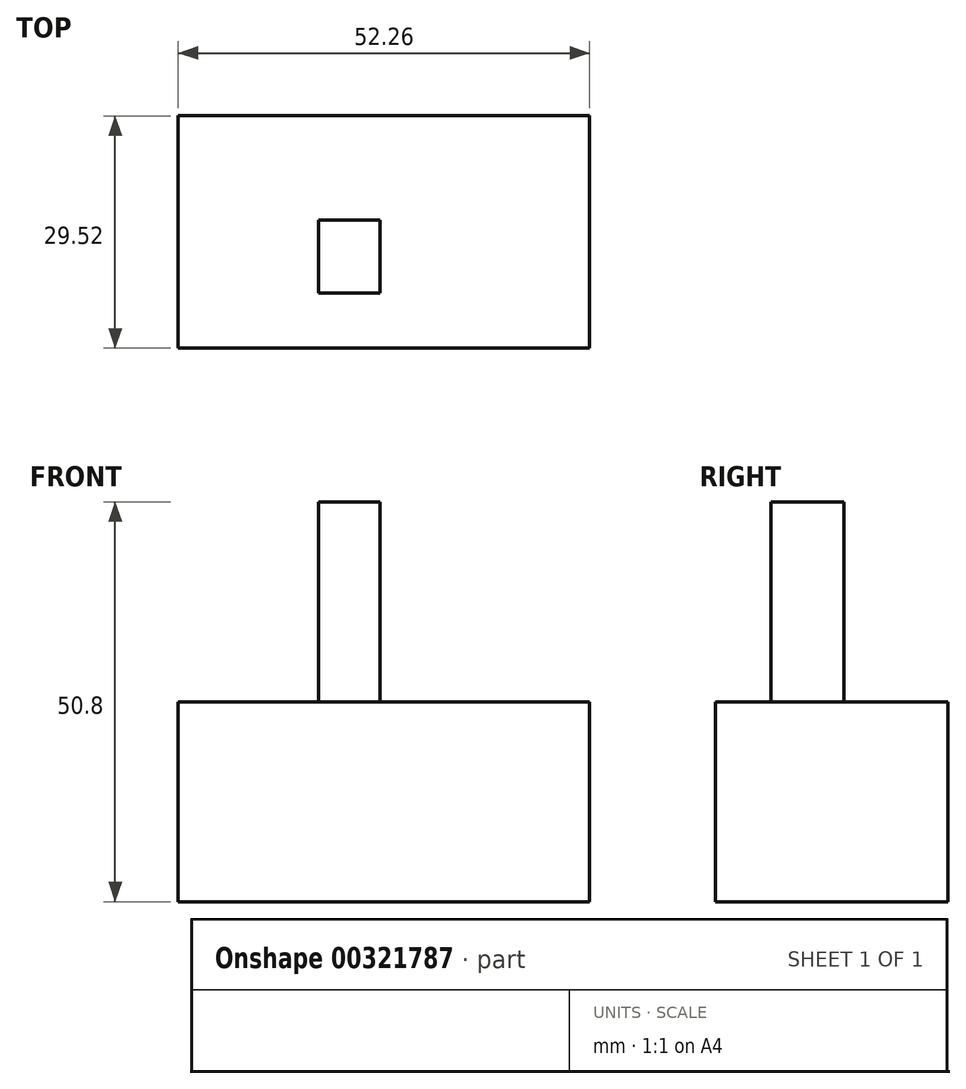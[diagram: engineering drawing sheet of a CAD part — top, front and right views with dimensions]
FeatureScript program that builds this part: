
annotation { "Feature Type Name" : "Feature", "Feature Type Description" : "" }
export const myFeature = defineFeature(function(context is Context, id is Id, definition is map)
    precondition{}
    {
        {
            var Q0;
            Q0=qCreatedBy(makeId("Top.planeOp"),FACE);
            var sketch = newSketch(context, id + "F0", { "sketchPlane" : qUnion([Q0])});
            skLineSegment(sketch, "E0.bottom", {"start": v(0, 0) * mm, "end": v(52.26, 0) * mm});
            skLineSegment(sketch, "E0.top", {"start": v(0, 29.52) * mm, "end": v(52.26, 29.52) * mm});
            skLineSegment(sketch, "E0.left", {"start": v(0, 0) * mm, "end": v(0, 29.52) * mm});
            skLineSegment(sketch, "E0.right", {"start": v(52.26, 0) * mm, "end": v(52.26, 29.52) * mm});
            skSolve(sketch);
        }
        {
            var Q0;
            Q0 = qSketchRegion(id + "F0", true);
            extrude(context, id + "F1", {"entities" : qUnion([Q0]), "depth" : 25.4 * mm});
        }
        {
            var Q0;
            Q0=makeQuery(id+"F1.opExtrude","CAP_FACE",FACE,{"disambiguationData":[OSD([sQuery(id+"F0.wireOp",EDGE,"E0.bottom"),sQuery(id+"F0.wireOp",EDGE,"E0.top"),sQuery(id+"F0.wireOp",EDGE,"E0.left"),sQuery(id+"F0.wireOp",EDGE,"E0.right")])],"isStart":false});
            var sketch = newSketch(context, id + "F2", { "sketchPlane" : qUnion([Q0])});
            skText(sketch, "E1", { "text": "諺呈\n", "fontName": "OpenSans-Regular.ttf"});
            const initialGuessF2  = {"E1": [0.00797, 0.0062, 1, 0, 0.01092]};
            skSetInitialGuess(sketch, initialGuessF2);
            skSolve(sketch);
        }
        {
            var Q0;
            Q0=makeQuery(id+"F2.imprint","IMPRINT",FACE,{"disambiguationData":[TD([[makeQuery(id+"F2.imprint","IMPRINT",EDGE,{"derivedFrom":sQuery(id+"F2.wireOp",EDGE,"E1.sketch_text.stroke-4")}),1.0]])]});
            extrude(context, id + "F3", {"entities" : qUnion([Q0]), "operationType" : NewBodyOperationType.ADD, "depth" : 25.4 * mm});
        }
    });
